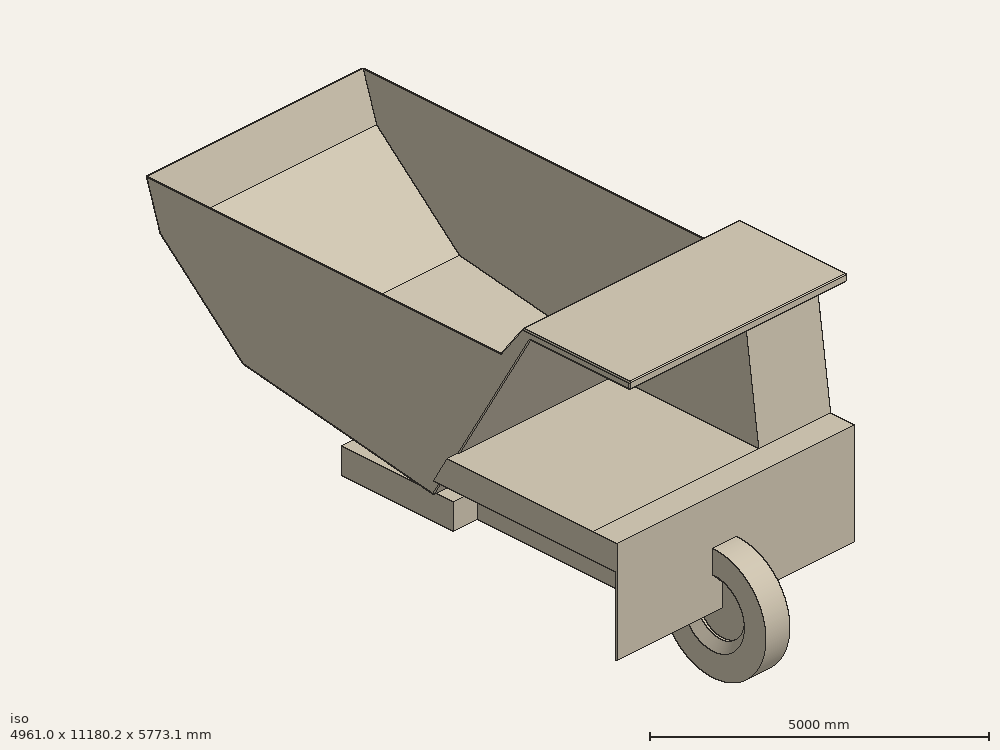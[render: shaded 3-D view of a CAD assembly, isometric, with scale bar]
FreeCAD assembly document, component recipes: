
FREECAD ASSEMBLY — COMPONENT RECIPES ("parts")

This assembly document has 7 components, labeled P0..P6 below (a component is one placed body or linked part). 7 of them carry a construction recipe — the FreeCAD feature program that regenerates the part from scratch, quoted from this document or its linked companion documents; the rest are supplied as boundary geometry only. No exploded tour is included for this assembly.
COMPONENT P0 — recipe-attached ("bodypart", modeled in this document).
Construction recipe (the document's own serialized feature program — sketch geometry with constraints, then the solid features built on it; lengths are millimeters unless a unit is written):

FEATURE [Sketcher::SketchObject] Sketch
  FullyConstrained = true
  MapMode = 5
  Placement = pos=(0,0,0) rot=(0.57735,0.57735,0.57735;2.0944rad)
  Support = -> [YZ_Plane]
  sketch-geometry (9):
    g0: LineSegment StartX=0 StartY=0 StartZ=0 EndX=4570 EndY=0 EndZ=0
    g1: LineSegment StartX=4570 StartY=0 StartZ=0 EndX=4558.22 EndY=500 EndZ=0
    g2: LineSegment StartX=4558.22 StartY=500 StartZ=0 EndX=2220.73 EndY=500 EndZ=0
    g3: LineSegment StartX=2220.73 StartY=500 StartZ=0 EndX=200 EndY=4000 EndZ=0
    g4: LineSegment StartX=200 StartY=4000 StartZ=0 EndX=-1416.39 EndY=4000 EndZ=0
    g5: LineSegment StartX=-1416.39 StartY=4000 StartZ=0 EndX=-1690 EndY=2000 EndZ=0
    g6: LineSegment StartX=-1690 StartY=2000 StartZ=0 EndX=-2190 EndY=2000 EndZ=0
    g7: LineSegment StartX=-2190 StartY=2000 StartZ=0 EndX=-2190 EndY=0 EndZ=0
    g8: LineSegment StartX=-2190 StartY=0 StartZ=0 EndX=0 EndY=0 EndZ=0
  constraints (26):
    c: Coincident(g0,g-1)
    c: PointOnObject(g0,g-1)
    c: Coincident(g1,g0)
    c: Coincident(g4,g3)
    c: Horizontal(g4)
    c: Coincident(g5,g4)
    c: Horizontal(g6)
    c: PointOnObject(g8,g-1)
    c: Coincident(g8,g0)
    c: Coincident(g6,g7)
    c: Coincident(g6,g5)
    c: Coincident(g3,g2)
    c: Coincident(g1,g2)
    c: DistanceX(g0,g0) = 4570
    c: DistanceX(g8,g0) = 2190
    c: DistanceY(g0,g1) = 500
    c: Parallel(g2,g0)
    c: Angle(g8,g7) = 1.5708
    c: DistanceY(g8,g6) = 2000
    c: DistanceY(g6,g4) = 2000
    c: DistanceX(g0,g3) = 200
    c: Angle(g5,g4) = 1.70676
    c: DistanceX(g6,g6) = 500
    c: Coincident(g7,g8)
    c: Angle(g4,g3) = 2.0944
    c: Angle(g2,g1) = 1.59436
FEATURE [PartDesign::Pad] Pad
  Direction = (1,-2e-16,3e-16)
  Length = 4961
  Length2 = 10
  Placement = pos=(0,0,0) rot=(0.57735,0.57735,0.57735;2.0944rad)
  Profile = -> Sketch
  ReferenceAxis = -> Sketch [N_Axis]
  Type = 0
FEATURE [Sketcher::SketchObject] Sketch001
  ExternalGeometry = -> [Pad]
  FullyConstrained = true
  MapMode = 5
  Placement = pos=(4961,-1.0914e-12,1.0914e-12) rot=(0.57735,0.57735,0.57735;2.0944rad)
  Support = -> [Pad]
  sketch-geometry (4):
    g0: LineSegment StartX=-2150 StartY=1500 StartZ=0 EndX=2220.73 EndY=1500 EndZ=0
    g1: LineSegment StartX=2220.73 StartY=1500 StartZ=0 EndX=2220.73 EndY=0 EndZ=0
    g2: LineSegment StartX=2220.73 StartY=0 StartZ=0 EndX=-2150 EndY=0 EndZ=0
    g3: LineSegment StartX=-2150 StartY=0 StartZ=0 EndX=-2150 EndY=1500 EndZ=0
  constraints (12):
    c: Coincident(g0,g1)
    c: Coincident(g1,g2)
    c: Coincident(g2,g3)
    c: Coincident(g3,g0)
    c: Horizontal(g0)
    c: Horizontal(g2)
    c: Vertical(g1)
    c: Vertical(g3)
    c: PointOnObject(g1,g-1)
    c: DistanceX(g-3,g2) = 40
    c: DistanceX(g-4,g1) = 0
    c: DistanceY(g2,g0) = 1500
FEATURE [PartDesign::Pocket] Pocket
  BaseFeature = -> Pad
  Direction = (-1,4e-16,-4e-16)
  Length = 1500
  Length2 = 5
  Placement = pos=(0,0,0) rot=(0.57735,0.57735,0.57735;2.0944rad)
  Profile = -> Sketch001
  ReferenceAxis = -> Sketch001 [N_Axis]
  Type = 0
FEATURE [Sketcher::SketchObject] Sketch002
  ExternalGeometry = -> [Pocket]
  FullyConstrained = true
  MapMode = 5
  Placement = pos=(-1.3e-15,0,0) rot=(0.57735,0.57735,-0.57735;4.18879rad)
  Support = -> [Pocket]
  sketch-geometry (4):
    g0: LineSegment StartX=-2150 StartY=-1.5916e-12 StartZ=0 EndX=2220.73 EndY=-1.5916e-12 EndZ=0
    g1: LineSegment StartX=2220.73 StartY=-1.5916e-12 StartZ=0 EndX=2220.73 EndY=-1500 EndZ=0
    g2: LineSegment StartX=2220.73 StartY=-1500 StartZ=0 EndX=-2150 EndY=-1500 EndZ=0
    g3: LineSegment StartX=-2150 StartY=-1500 StartZ=0 EndX=-2150 EndY=-1.5916e-12 EndZ=0
  constraints (12):
    c: Coincident(g0,g1)
    c: Coincident(g1,g2)
    c: Coincident(g2,g3)
    c: Coincident(g3,g0)
    c: Horizontal(g0)
    c: Horizontal(g2)
    c: Vertical(g1)
    c: Vertical(g3)
    c: DistanceX(g-3,g0) = 40
    c: DistanceY(g1,g0) = 1500
    c: DistanceY(g0,g-3) = 0
    c: DistanceX(g0,g-4) = 0
FEATURE [PartDesign::Pocket] Pocket001
  BaseFeature = -> Pocket
  Direction = (1,-6e-16,5e-16)
  Length = 1500
  Length2 = 5
  Placement = pos=(0,0,0) rot=(0.57735,0.57735,0.57735;2.0944rad)
  Profile = -> Sketch002
  ReferenceAxis = -> Sketch002 [N_Axis]
  Type = 0
FEATURE [Sketcher::SketchObject] Sketch003
  ExternalGeometry = -> [Pocket001]
  FullyConstrained = true
  MapMode = 5
  Placement = pos=(0,0,0) rot=(0.707107,0.707107,0;3.14159rad)
  Support = -> [Pocket001]
  sketch-geometry (8):
    g0: LineSegment StartX=4570 StartY=4961 StartZ=0 EndX=4570 EndY=3961 EndZ=0
    g1: LineSegment StartX=4570 StartY=3961 StartZ=0 EndX=2220.73 EndY=3961 EndZ=0
    g2: LineSegment StartX=2220.73 StartY=4961 StartZ=0 EndX=2220.73 EndY=3961 EndZ=0
    g3: LineSegment StartX=4570 StartY=0 StartZ=0 EndX=2220.73 EndY=0 EndZ=0
    g4: LineSegment StartX=2220.73 StartY=0 StartZ=0 EndX=2220.73 EndY=1000 EndZ=0
    g5: LineSegment StartX=2220.73 StartY=1000 StartZ=0 EndX=4570 EndY=1000 EndZ=0
    g6: LineSegment StartX=4570 StartY=1000 StartZ=0 EndX=4570 EndY=0 EndZ=0
    g7: LineSegment StartX=2220.73 StartY=4961 StartZ=0 EndX=4570 EndY=4961 EndZ=0
  constraints (21):
    c: Vertical(g0)
    c: Coincident(g1,g0)
    c: Horizontal(g1)
    c: Coincident(g2,g-3)
    c: Coincident(g2,g1)
    c: Vertical(g2)
    c: Coincident(g0,g-3)
    c: DistanceY(g0,g0) = 1000
    c: Coincident(g3,g4)
    c: Coincident(g4,g5)
    c: Coincident(g5,g6)
    c: Coincident(g6,g3)
    c: Horizontal(g3)
    c: Horizontal(g5)
    c: Vertical(g4)
    c: Vertical(g6)
    c: Coincident(g3,g-5)
    c: PointOnObject(g4,g-6)
    c: DistanceY(g3,g5) = 1000
    c: Coincident(g7,g2)
    c: Coincident(g7,g0)
FEATURE [PartDesign::Pocket] Pocket002
  BaseFeature = -> Pocket001
  Direction = (-1.1e-15,8e-16,1)
  Length = 2000
  Length2 = 5
  Placement = pos=(0,0,0) rot=(0.57735,0.57735,0.57735;2.0944rad)
  Profile = -> Sketch003
  ReferenceAxis = -> Sketch003 [N_Axis]
  Type = 0
FEATURE [Sketcher::SketchObject] Sketch006
  ExternalGeometry = -> [Pocket002]
  FullyConstrained = true
  MapMode = 5
  Placement = pos=(-9.338e-13,-1927.54,263.697) rot=(0.549352,0.549352,-0.629623;2.01776rad)
  Support = -> [Pocket002]
  sketch-geometry (4):
    g0: LineSegment StartX=-3771.1 StartY=1.3642e-12 StartZ=0 EndX=-1752.48 EndY=1.3642e-12 EndZ=0
    g1: LineSegment StartX=-1752.48 StartY=1.3642e-12 StartZ=0 EndX=-1752.48 EndY=3461 EndZ=0
    g2: LineSegment StartX=-1752.48 StartY=3461 StartZ=0 EndX=-3771.1 EndY=3461 EndZ=0
    g3: LineSegment StartX=-3771.1 StartY=3461 StartZ=0 EndX=-3771.1 EndY=1.3642e-12 EndZ=0
  constraints (11):
    c: Coincident(g0,g1)
    c: Coincident(g1,g2)
    c: Coincident(g2,g3)
    c: Coincident(g3,g0)
    c: Horizontal(g0)
    c: Horizontal(g2)
    c: Vertical(g1)
    c: Vertical(g3)
    c: Coincident(g-3,g0)
    c: DistanceY(g2,g-4) = 1500
    c: DistanceX(g0,g-5) = 0
FEATURE [PartDesign::Pocket] Pocket003
  AlongSketchNormal = false
  BaseFeature = -> Pocket002
  Direction = (0,0.1,0)
  Length = 2000
  Length2 = 5
  Placement = pos=(0,0,0) rot=(0.57735,0.57735,0.57735;2.0944rad)
  Profile = -> Sketch006
  ReferenceAxis = -> Sketch006 [N_Axis]
  Type = 1
  UseCustomVector = true
FEATURE [PartDesign::Body] Body
  Group = -> [Sketch,Pad,Sketch001,Pocket,Sketch002,Pocket001,Sketch003,Pocket002,Sketch006,Pocket003]
  Origin = -> Origin
  Placement = pos=(-2500,2200,0) rot=(0,0,1;0rad)
  Tip = -> Pocket003
COMPONENT P1 — recipe-attached ("real_back_left_wheel_", modeled in this document).
Construction recipe (the document's own serialized feature program — sketch geometry with constraints, then the solid features built on it; lengths are millimeters unless a unit is written):

FEATURE [Sketcher::SketchObject] Sketch007
  FullyConstrained = true
  MapMode = 5
  Placement = pos=(0,0,0) rot=(0.57735,0.57735,0.57735;2.0944rad)
  Support = -> [YZ_Plane004]
  sketch-geometry (1):
    g0: Circle CenterX=0 CenterY=0 CenterZ=0 NormalX=0 NormalY=0 NormalZ=1 AngleXU=0 Radius=1100.04
  constraints (2):
    c: Coincident(g0,g-1)
    c: Radius(g0) = 1100.04
FEATURE [PartDesign::Pad] Pad002
  Direction = (1,-2e-16,3e-16)
  Length = 500
  Length2 = 10
  Placement = pos=(0,0,0) rot=(0.57735,0.57735,0.57735;2.0944rad)
  Profile = -> Sketch007
  ReferenceAxis = -> Sketch007 [N_Axis]
  Type = 0
FEATURE [Sketcher::SketchObject] Sketch008
  ExternalGeometry = -> [Pad002]
  FullyConstrained = true
  MapMode = 5
  Placement = pos=(0,0,0) rot=(0.57735,0.57735,-0.57735;4.18879rad)
  Support = -> [Pad002]
  sketch-geometry (1):
    g0: Circle CenterX=0 CenterY=0 CenterZ=0 NormalX=0 NormalY=0 NormalZ=1 AngleXU=0 Radius=500
  constraints (2):
    c: Coincident(g0,g-3)
    c: Radius(g0) = 500
FEATURE [PartDesign::Pocket] Pocket004
  BaseFeature = -> Pad002
  Direction = (1,-4e-16,4e-16)
  Length = 200
  Length2 = 5
  Placement = pos=(0,0,0) rot=(0.57735,0.57735,0.57735;2.0944rad)
  Profile = -> Sketch008
  ReferenceAxis = -> Sketch008 [N_Axis]
  Type = 0
FEATURE [PartDesign::Chamfer] Chamfer
  Angle = 45
  Base = -> Pocket004 [Edge4]
  BaseFeature = -> Pocket004
  ChamferType = 0
  FlipDirection = false
  Placement = pos=(0,0,0) rot=(0.57735,0.57735,0.57735;2.0944rad)
  Size = 150
  Size2 = 1
  SupportTransform = false
  UseAllEdges = false
FEATURE [PartDesign::Body] Body003  label="Wheel"
  Group = -> [Sketch007,Pad002,Sketch008,Pocket004,Chamfer]
  Origin = -> Origin004
  Placement = pos=(-500,0,0) rot=(0,0,1;0rad)
  Tip = -> Chamfer
COMPONENT P2 — same part as P1; its construction recipe is shown at P1.
COMPONENT P3 — recipe-attached ("real_body_", modeled in this document).
Construction recipe (the document's own serialized feature program — sketch geometry with constraints, then the solid features built on it; lengths are millimeters unless a unit is written):

FEATURE [Sketcher::SketchObject] Sketch
  FullyConstrained = true
  MapMode = 5
  Placement = pos=(0,0,0) rot=(0.57735,0.57735,0.57735;2.0944rad)
  Support = -> [YZ_Plane]
  sketch-geometry (9):
    g0: LineSegment StartX=0 StartY=0 StartZ=0 EndX=4570 EndY=0 EndZ=0
    g1: LineSegment StartX=4570 StartY=0 StartZ=0 EndX=4558.22 EndY=500 EndZ=0
    g2: LineSegment StartX=4558.22 StartY=500 StartZ=0 EndX=2220.73 EndY=500 EndZ=0
    g3: LineSegment StartX=2220.73 StartY=500 StartZ=0 EndX=200 EndY=4000 EndZ=0
    g4: LineSegment StartX=200 StartY=4000 StartZ=0 EndX=-1416.39 EndY=4000 EndZ=0
    g5: LineSegment StartX=-1416.39 StartY=4000 StartZ=0 EndX=-1690 EndY=2000 EndZ=0
    g6: LineSegment StartX=-1690 StartY=2000 StartZ=0 EndX=-2190 EndY=2000 EndZ=0
    g7: LineSegment StartX=-2190 StartY=2000 StartZ=0 EndX=-2190 EndY=0 EndZ=0
    g8: LineSegment StartX=-2190 StartY=0 StartZ=0 EndX=0 EndY=0 EndZ=0
  constraints (26):
    c: Coincident(g0,g-1)
    c: PointOnObject(g0,g-1)
    c: Coincident(g1,g0)
    c: Coincident(g4,g3)
    c: Horizontal(g4)
    c: Coincident(g5,g4)
    c: Horizontal(g6)
    c: PointOnObject(g8,g-1)
    c: Coincident(g8,g0)
    c: Coincident(g6,g7)
    c: Coincident(g6,g5)
    c: Coincident(g3,g2)
    c: Coincident(g1,g2)
    c: DistanceX(g0,g0) = 4570
    c: DistanceX(g8,g0) = 2190
    c: DistanceY(g0,g1) = 500
    c: Parallel(g2,g0)
    c: Angle(g8,g7) = 1.5708
    c: DistanceY(g8,g6) = 2000
    c: DistanceY(g6,g4) = 2000
    c: DistanceX(g0,g3) = 200
    c: Angle(g5,g4) = 1.70676
    c: DistanceX(g6,g6) = 500
    c: Coincident(g7,g8)
    c: Angle(g4,g3) = 2.0944
    c: Angle(g2,g1) = 1.59436
FEATURE [PartDesign::Pad] Pad
  Direction = (1,-2e-16,3e-16)
  Length = 4961
  Length2 = 10
  Placement = pos=(0,0,0) rot=(0.57735,0.57735,0.57735;2.0944rad)
  Profile = -> Sketch
  ReferenceAxis = -> Sketch [N_Axis]
  Type = 0
FEATURE [Sketcher::SketchObject] Sketch001
  ExternalGeometry = -> [Pad]
  FullyConstrained = true
  MapMode = 5
  Placement = pos=(4961,-1.0914e-12,1.0914e-12) rot=(0.57735,0.57735,0.57735;2.0944rad)
  Support = -> [Pad]
  sketch-geometry (4):
    g0: LineSegment StartX=-2150 StartY=1500 StartZ=0 EndX=2220.73 EndY=1500 EndZ=0
    g1: LineSegment StartX=2220.73 StartY=1500 StartZ=0 EndX=2220.73 EndY=0 EndZ=0
    g2: LineSegment StartX=2220.73 StartY=0 StartZ=0 EndX=-2150 EndY=0 EndZ=0
    g3: LineSegment StartX=-2150 StartY=0 StartZ=0 EndX=-2150 EndY=1500 EndZ=0
  constraints (12):
    c: Coincident(g0,g1)
    c: Coincident(g1,g2)
    c: Coincident(g2,g3)
    c: Coincident(g3,g0)
    c: Horizontal(g0)
    c: Horizontal(g2)
    c: Vertical(g1)
    c: Vertical(g3)
    c: PointOnObject(g1,g-1)
    c: DistanceX(g-3,g2) = 40
    c: DistanceX(g-4,g1) = 0
    c: DistanceY(g2,g0) = 1500
FEATURE [PartDesign::Pocket] Pocket
  BaseFeature = -> Pad
  Direction = (-1,4e-16,-4e-16)
  Length = 1500
  Length2 = 5
  Placement = pos=(0,0,0) rot=(0.57735,0.57735,0.57735;2.0944rad)
  Profile = -> Sketch001
  ReferenceAxis = -> Sketch001 [N_Axis]
  Type = 0
FEATURE [Sketcher::SketchObject] Sketch002
  ExternalGeometry = -> [Pocket]
  FullyConstrained = true
  MapMode = 5
  Placement = pos=(-1.3e-15,0,0) rot=(0.57735,0.57735,-0.57735;4.18879rad)
  Support = -> [Pocket]
  sketch-geometry (4):
    g0: LineSegment StartX=-2150 StartY=-1.5916e-12 StartZ=0 EndX=2220.73 EndY=-1.5916e-12 EndZ=0
    g1: LineSegment StartX=2220.73 StartY=-1.5916e-12 StartZ=0 EndX=2220.73 EndY=-1500 EndZ=0
    g2: LineSegment StartX=2220.73 StartY=-1500 StartZ=0 EndX=-2150 EndY=-1500 EndZ=0
    g3: LineSegment StartX=-2150 StartY=-1500 StartZ=0 EndX=-2150 EndY=-1.5916e-12 EndZ=0
  constraints (12):
    c: Coincident(g0,g1)
    c: Coincident(g1,g2)
    c: Coincident(g2,g3)
    c: Coincident(g3,g0)
    c: Horizontal(g0)
    c: Horizontal(g2)
    c: Vertical(g1)
    c: Vertical(g3)
    c: DistanceX(g-3,g0) = 40
    c: DistanceY(g1,g0) = 1500
    c: DistanceY(g0,g-3) = 0
    c: DistanceX(g0,g-4) = 0
FEATURE [PartDesign::Pocket] Pocket001
  BaseFeature = -> Pocket
  Direction = (1,-6e-16,5e-16)
  Length = 1500
  Length2 = 5
  Placement = pos=(0,0,0) rot=(0.57735,0.57735,0.57735;2.0944rad)
  Profile = -> Sketch002
  ReferenceAxis = -> Sketch002 [N_Axis]
  Type = 0
FEATURE [Sketcher::SketchObject] Sketch003
  ExternalGeometry = -> [Pocket001]
  FullyConstrained = true
  MapMode = 5
  Placement = pos=(0,0,0) rot=(0.707107,0.707107,0;3.14159rad)
  Support = -> [Pocket001]
  sketch-geometry (8):
    g0: LineSegment StartX=4570 StartY=4961 StartZ=0 EndX=4570 EndY=3961 EndZ=0
    g1: LineSegment StartX=4570 StartY=3961 StartZ=0 EndX=2220.73 EndY=3961 EndZ=0
    g2: LineSegment StartX=2220.73 StartY=4961 StartZ=0 EndX=2220.73 EndY=3961 EndZ=0
    g3: LineSegment StartX=4570 StartY=0 StartZ=0 EndX=2220.73 EndY=0 EndZ=0
    g4: LineSegment StartX=2220.73 StartY=0 StartZ=0 EndX=2220.73 EndY=1000 EndZ=0
    g5: LineSegment StartX=2220.73 StartY=1000 StartZ=0 EndX=4570 EndY=1000 EndZ=0
    g6: LineSegment StartX=4570 StartY=1000 StartZ=0 EndX=4570 EndY=0 EndZ=0
    g7: LineSegment StartX=2220.73 StartY=4961 StartZ=0 EndX=4570 EndY=4961 EndZ=0
  constraints (21):
    c: Vertical(g0)
    c: Coincident(g1,g0)
    c: Horizontal(g1)
    c: Coincident(g2,g-3)
    c: Coincident(g2,g1)
    c: Vertical(g2)
    c: Coincident(g0,g-3)
    c: DistanceY(g0,g0) = 1000
    c: Coincident(g3,g4)
    c: Coincident(g4,g5)
    c: Coincident(g5,g6)
    c: Coincident(g6,g3)
    c: Horizontal(g3)
    c: Horizontal(g5)
    c: Vertical(g4)
    c: Vertical(g6)
    c: Coincident(g3,g-5)
    c: PointOnObject(g4,g-6)
    c: DistanceY(g3,g5) = 1000
    c: Coincident(g7,g2)
    c: Coincident(g7,g0)
FEATURE [PartDesign::Pocket] Pocket002
  BaseFeature = -> Pocket001
  Direction = (-1.1e-15,8e-16,1)
  Length = 2000
  Length2 = 5
  Placement = pos=(0,0,0) rot=(0.57735,0.57735,0.57735;2.0944rad)
  Profile = -> Sketch003
  ReferenceAxis = -> Sketch003 [N_Axis]
  Type = 0
FEATURE [Sketcher::SketchObject] Sketch006
  ExternalGeometry = -> [Pocket002]
  FullyConstrained = true
  MapMode = 5
  Placement = pos=(-9.338e-13,-1927.54,263.697) rot=(0.549352,0.549352,-0.629623;2.01776rad)
  Support = -> [Pocket002]
  sketch-geometry (4):
    g0: LineSegment StartX=-3771.1 StartY=1.3642e-12 StartZ=0 EndX=-1752.48 EndY=1.3642e-12 EndZ=0
    g1: LineSegment StartX=-1752.48 StartY=1.3642e-12 StartZ=0 EndX=-1752.48 EndY=3461 EndZ=0
    g2: LineSegment StartX=-1752.48 StartY=3461 StartZ=0 EndX=-3771.1 EndY=3461 EndZ=0
    g3: LineSegment StartX=-3771.1 StartY=3461 StartZ=0 EndX=-3771.1 EndY=1.3642e-12 EndZ=0
  constraints (11):
    c: Coincident(g0,g1)
    c: Coincident(g1,g2)
    c: Coincident(g2,g3)
    c: Coincident(g3,g0)
    c: Horizontal(g0)
    c: Horizontal(g2)
    c: Vertical(g1)
    c: Vertical(g3)
    c: Coincident(g-3,g0)
    c: DistanceY(g2,g-4) = 1500
    c: DistanceX(g0,g-5) = 0
FEATURE [PartDesign::Pocket] Pocket003
  AlongSketchNormal = false
  BaseFeature = -> Pocket002
  Direction = (0,0.1,0)
  Length = 2000
  Length2 = 5
  Placement = pos=(0,0,0) rot=(0.57735,0.57735,0.57735;2.0944rad)
  Profile = -> Sketch006
  ReferenceAxis = -> Sketch006 [N_Axis]
  Type = 1
  UseCustomVector = true
FEATURE [PartDesign::Body] Body
  Group = -> [Sketch,Pad,Sketch001,Pocket,Sketch002,Pocket001,Sketch003,Pocket002,Sketch006,Pocket003]
  Origin = -> Origin
  Placement = pos=(-2500,2200,0) rot=(0,0,1;0rad)
  Tip = -> Pocket003
COMPONENT P4 — same part as P1; its construction recipe is shown at P1.
COMPONENT P5 — same part as P1; its construction recipe is shown at P1.
COMPONENT P6 — recipe-attached ("real_tray_", modeled in this document).
Construction recipe (the document's own serialized feature program — sketch geometry with constraints, then the solid features built on it; lengths are millimeters unless a unit is written):

FEATURE [Sketcher::SketchObject] Sketch004
  FullyConstrained = false
  MapMode = 5
  Placement = pos=(0,0,0) rot=(0.57735,0.57735,0.57735;2.0944rad)
  Support = -> [YZ_Plane001]
  sketch-geometry (9):
    g0: LineSegment StartX=-1708.54 StartY=4253.06 StartZ=0 EndX=-1708.54 EndY=4153.06 EndZ=0
    g1: LineSegment StartX=-1708.54 StartY=4153.06 StartZ=0 EndX=366.583 EndY=4153.06 EndZ=0
    g2: LineSegment StartX=366.583 StartY=4153.06 StartZ=0 EndX=2384.55 EndY=695.566 EndZ=0
    g3: LineSegment StartX=2384.55 StartY=695.566 StartZ=0 EndX=6349.97 EndY=1294.79 EndZ=0
    g4: LineSegment StartX=6349.97 StartY=1294.79 StartZ=0 EndX=8076.46 EndY=2810.46 EndZ=0
    g5: LineSegment StartX=8076.46 StartY=2810.46 StartZ=0 EndX=8359.11 EndY=3656.41 EndZ=0
    g6: LineSegment StartX=8359.11 StartY=3656.41 StartZ=0 EndX=948.185 EndY=3656.41 EndZ=0
    g7: LineSegment StartX=948.185 StartY=3656.41 StartZ=0 EndX=498.263 EndY=4253.06 EndZ=0
    g8: LineSegment StartX=498.263 StartY=4253.06 StartZ=0 EndX=-1708.54 EndY=4253.06 EndZ=0
  constraints (15):
    c: Coincident(g0,g1)
    c: Coincident(g1,g2)
    c: Coincident(g2,g3)
    c: Coincident(g3,g4)
    c: Coincident(g4,g5)
    c: Coincident(g5,g6)
    c: Horizontal(g6)
    c: Coincident(g6,g7)
    c: Coincident(g7,g8)
    c: Coincident(g8,g0)
    c: Horizontal(g8)
    c: DistanceX(g0,g4) = 9785
    c: Angle(g1,g0) = 1.5708
    c: DistanceY(g0,g0) = 100
    c: DistanceY(g1,g7) = 100
FEATURE [PartDesign::Pad] Pad001
  Direction = (1,-2e-16,3e-16)
  Length = 4500
  Length2 = 10
  Placement = pos=(0,0,0) rot=(0.57735,0.57735,0.57735;2.0944rad)
  Profile = -> Sketch004
  ReferenceAxis = -> Sketch004 [N_Axis]
  Type = 0
FEATURE [Sketcher::SketchObject] Sketch005
  FullyConstrained = true
  MapMode = 5
  Support = -> [XY_Plane001]
FEATURE [PartDesign::Thickness] Thickness
  Base = -> Pad001 [Face7]
  BaseFeature = -> Pad001
  Intersection = false
  Join = 0
  Mode = 0
  SupportTransform = false
  Value = 20
FEATURE [PartDesign::Body] Body001  label="Tray23"
  AttachedBy = Origin
  AttachedTo = Parent Assembly#LCS_Origin
  AttachmentOffset = pos=(-2250,1700,400) rot=(0,0,1;0rad)
  Group = -> [Sketch004,Pad001,Thickness,Sketch005]
  Origin = -> Origin001
  Placement = pos=(-2250,1700,400) rot=(0,0,1;0rad)
  SolverId = Asm4EE
  Tip = -> Thickness
  expr: Placement = LCS_Origin.Placement * AttachmentOffset
PROVENANCE & LICENSES
A FreeCAD (.FCStd) document from a public repository crawl; recipes are the document's own serialized feature recipes (and, for linked parts, companion documents' recipes).
License: bsd.
